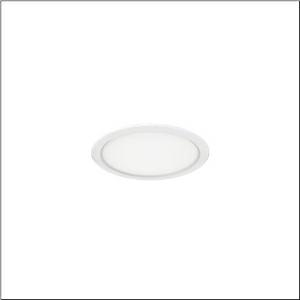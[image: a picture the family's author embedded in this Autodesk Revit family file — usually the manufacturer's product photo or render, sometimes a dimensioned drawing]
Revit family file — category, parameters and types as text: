
# Revit family: lunis_41_eco_51ds107d43b
name_source: partatom
category: Lighting Fixtures
units: mm (PartAtom-declared; Revit-internal decimal feet)

## family parameters
Cut with Voids When Loaded = No
Host = Face
Light Source = No
Part Type = Normal
Room Calculation Point = No
Round Connector Dimension = Use Diameter
Shared = No

## types (1)
- Lunis 41 Eco (1 x LED, 1580 lm, 12 W, 4000K)
    Apparent Load = 12 VA
    CIE Flux Codes = 47 80 97 100 100
    Color Rendering = 80
    Color Temperature = 4000K
    Default Elevation = 1800 mm
    Description = Lunis 41 Eco, downlight, light emission: direct distribution, LED rated luminous flux: 1.580lm, light colour: 840, mains connection: 230V, AC, 50/60Hz, housing, round, of aluminium, coated, traffic white (RAL 9016), diameter: 166mm, recess depth: 54mm, protection rating (complete): IP20, protection rating (on room side): IP40, insulation class (complete): insulation class II (safety insulation), certification: CE, permissible ambient temperature for indoor applications: -20..+40°C, packaging unit: 1 piece
    Height = 0 mm  [stored 0 ft]
    Lamp = 1 x LED
    Lamp Light Flux = 1580 lm
    Lamp Power = 12 W
    Lamp count = 1
    Length = 166 mm
    Luminous efficacy = 132 lm/W
    Manufacturer = Siteco
    ModVariant = No
    Model = 51DS107D43B
    Mounting Place = Ceiling
    Mounting Type = Recessed
    Number of Poles = 1
    OnlyDefault = Yes
    Power Factor = 1
    Product Name = Lunis 41 Eco
    Product group = downlight
    ProductGroupID = 401
    Protection Class = Protection class II
    Protection Degree = IP 20
    RLX_Detail_Level = 1
    RLX_Emergency_Light_Flux = 0 lm
    RLX_Emergency_Type = 0
    RLX_Emergency_Type_DB = No
    RlxData = <blob elided: 8877 chars, md5=7a800f18>
    Socket = socket
    Standby Power = 0 W
    System Light Flux = 1580 lm
    System Power = 12 W
    Type Comments = Product without accessories
    Type Image = l_1345912.jpg
    URL = http://relux.com
    VarID = ---
    Voltage = 0 V
    Weight = 0.00 kg
    Width = 0 mm  [stored 0 ft]

note: [stored X ft] marks values corroborated as IEEE doubles in the binary element streams (Revit-internal decimal feet)

## geometry (parser evidence)
native form markers: Sweep x8
no freeform markers — native parametric forms only
